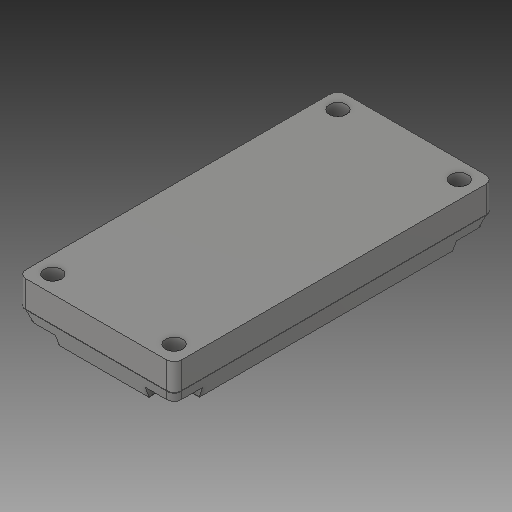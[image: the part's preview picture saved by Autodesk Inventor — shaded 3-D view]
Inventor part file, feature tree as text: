
AUTODESK INVENTOR PART (.ipt)
format: ipt  version: 2017 (Build 210142000, 142)  size: 163,328 bytes
history: native  units: in
note: dims shown in document units (in); Inventor stores cm internally (conversion verified against a paired STEP export)
features: fillet x1
ambient origin geometry x8: Origin, YZ Plane, XZ Plane, XY Plane, X Axis, Y Axis, Z Axis, Center Point
bodies: Solid1 (feature_tree)
feature tree (1):
  fillet  "Fillet2"  [1 undecoded]
note: 1 required parameter value undecoded (feature->parameter linkage not recoverable at this tier; creation-order binding heuristic only, values carry confidence <= 0.55)
